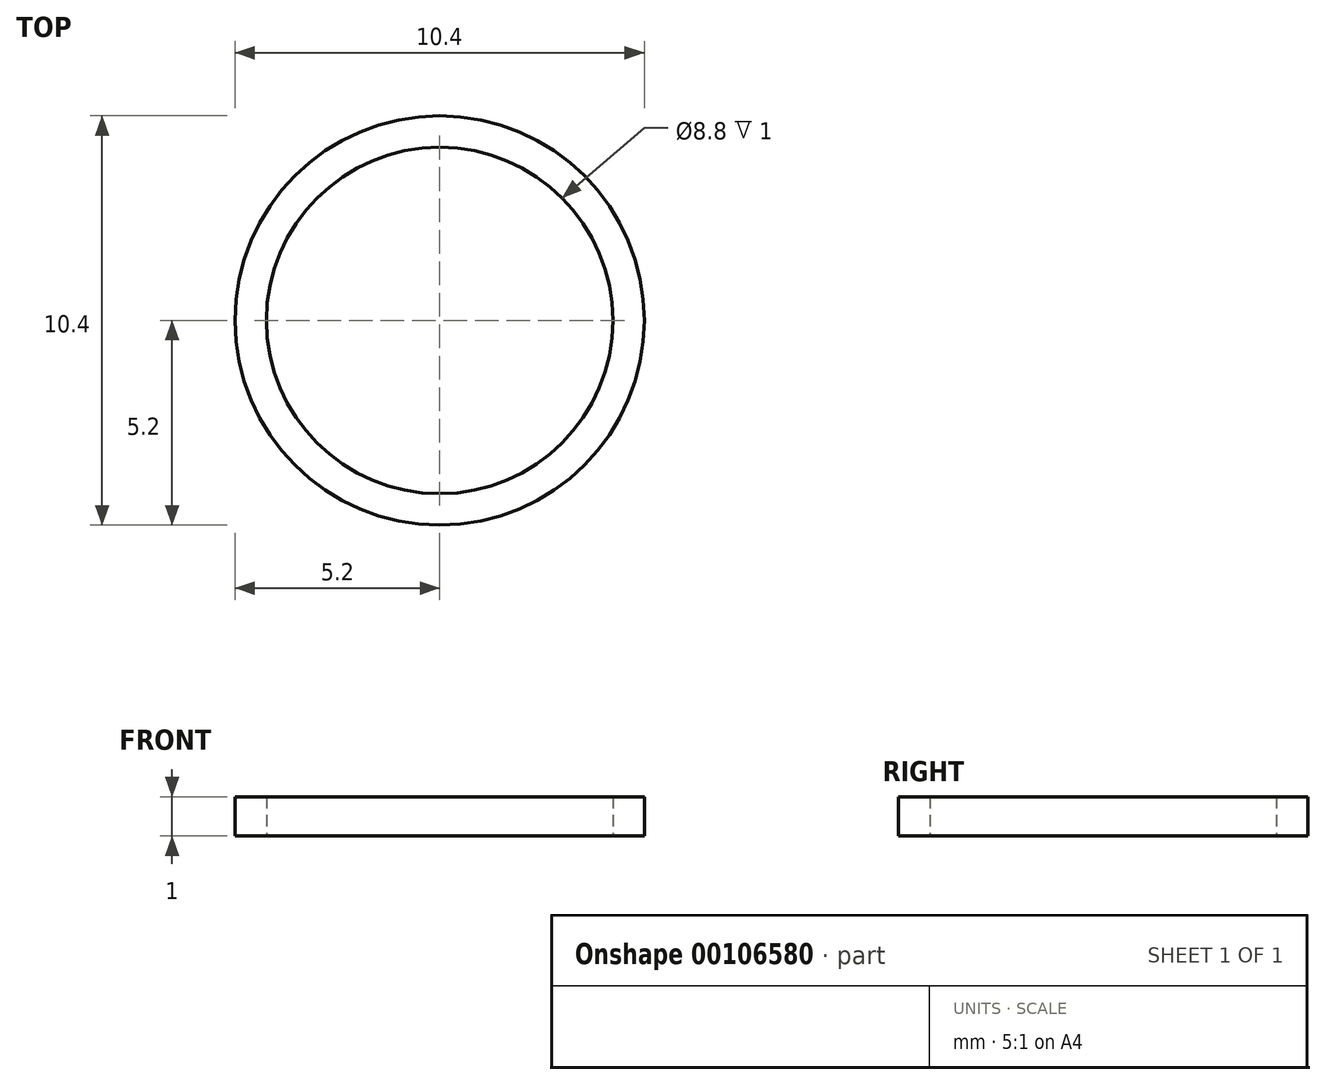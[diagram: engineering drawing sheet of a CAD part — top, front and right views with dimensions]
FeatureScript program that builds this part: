
annotation { "Feature Type Name" : "Feature", "Feature Type Description" : "" }
export const myFeature = defineFeature(function(context is Context, id is Id, definition is map)
    precondition{}
    {
        {
            var Q0;
            Q0=qCreatedBy(makeId("Top.planeOp"),FACE);
            var sketch = newSketch(context, id + "F0", { "sketchPlane" : qUnion([Q0])});
            skCircle(sketch, "E0", {"center": v(0, 0) * mm, "radius": 5.2 * mm});
            skCircle(sketch, "E1", {"center": v(0, 0) * mm, "radius": 4.4 * mm});
            skSolve(sketch);
        }
        {
            var Q0;
            Q0 = qSketchRegion(id + "F0", true);
            extrude(context, id + "F1", {"entities" : qUnion([Q0]), "depth" : 1 * mm});
        }
    });
